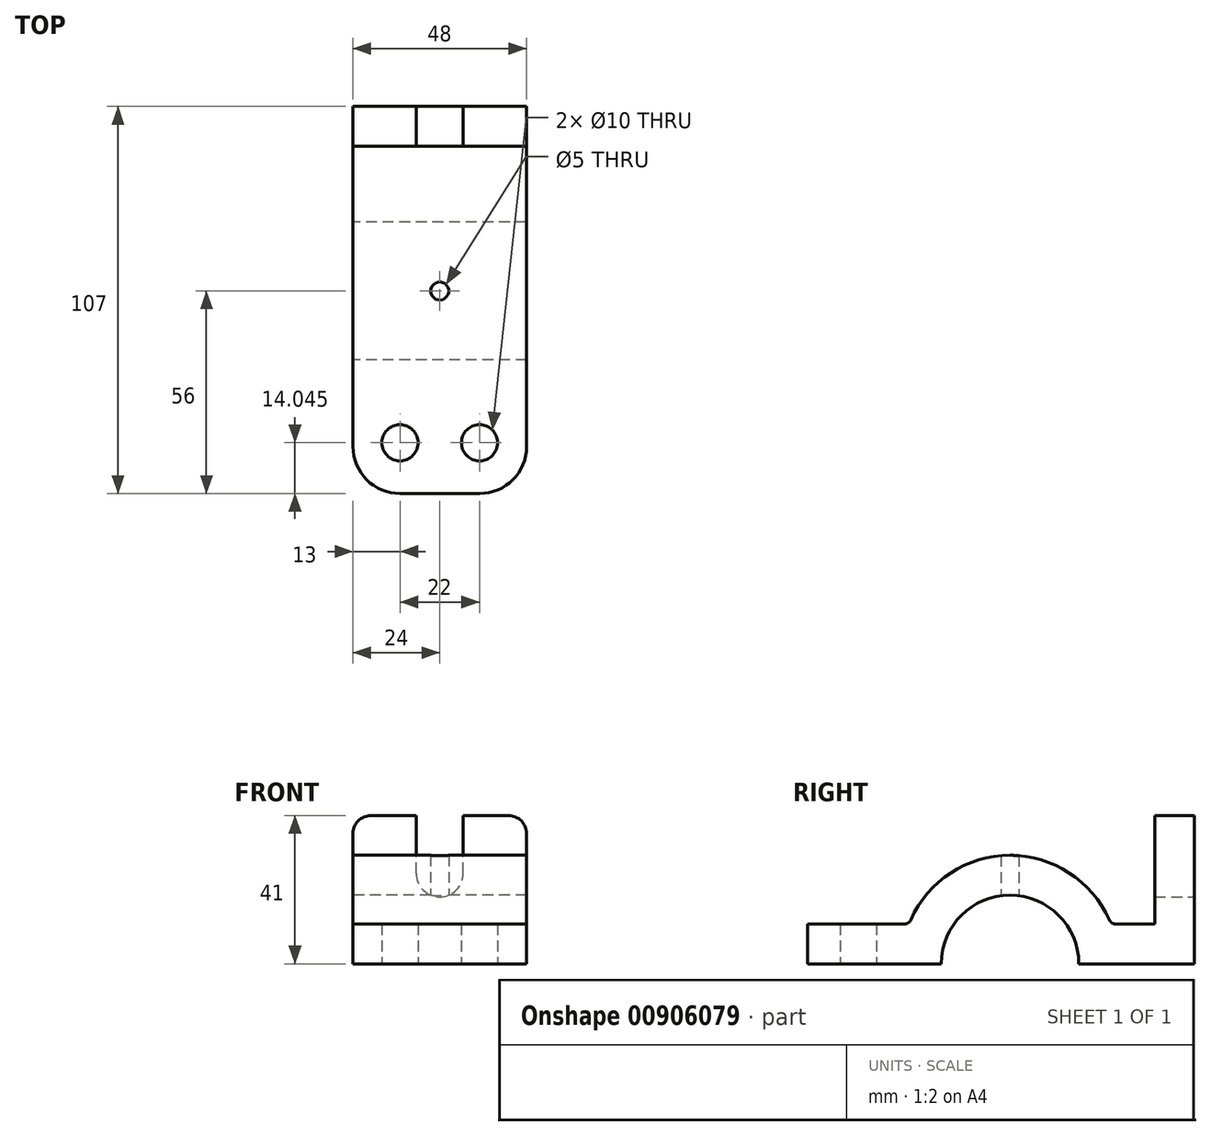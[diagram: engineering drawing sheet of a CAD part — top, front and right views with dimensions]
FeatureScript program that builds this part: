
annotation { "Feature Type Name" : "Feature", "Feature Type Description" : "" }
export const myFeature = defineFeature(function(context is Context, id is Id, definition is map)
    precondition{}
    {
        {
            var Q0;
            Q0=qCreatedBy(makeId("Right.planeOp"),FACE);
            var sketch = newSketch(context, id + "F0", { "sketchPlane" : qUnion([Q0])});
            skCircle(sketch, "E0", {"center": v(0, 0) * mm, "radius": 19 * mm});
            skCircle(sketch, "E1", {"center": v(0, 0) * mm, "radius": 30 * mm});
            skLineSegment(sketch, "E2.bottom", {"start": v(-56, 0) * mm, "end": v(51, 0) * mm});
            skLineSegment(sketch, "E2.top", {"start": v(-56, 11) * mm, "end": v(51, 11) * mm});
            skLineSegment(sketch, "E2.left", {"start": v(-56, 0) * mm, "end": v(-56, 11) * mm});
            skLineSegment(sketch, "E2.right", {"start": v(51, 0) * mm, "end": v(51, 11) * mm});
            skLineSegment(sketch, "E3.bottom", {"start": v(51, 11) * mm, "end": v(40, 11) * mm});
            skLineSegment(sketch, "E3.top", {"start": v(51, 41) * mm, "end": v(40, 41) * mm});
            skLineSegment(sketch, "E3.left", {"start": v(51, 11) * mm, "end": v(51, 41) * mm});
            skLineSegment(sketch, "E3.right", {"start": v(40, 11) * mm, "end": v(40, 41) * mm});
            skSolve(sketch);
        }
        {
            var Q0;
            {var subQ5=sQuery(id+"F0.wireOp",EDGE,"E2.left");Q0=makeQuery(id+"F0.imprint","IMPRINT",FACE,{"disambiguationData":[TD([[makeQuery(id+"F0.imprint","IMPRINT",EDGE,{"derivedFrom":subQ5}),-1.0]])]});}
            var Q1;
            {var subQ0=sQuery(id+"F0.wireOp",EDGE,"E2.bottom");var subQ1=sQuery(id+"F0.wireOp",EDGE,"E0");var subQ2=makeQuery(id+"F0.imprint","INTERSECT",VERTEX,{"disambiguationData":[OD(0.0)],"derivedFrom":[subQ1,subQ0]});Q1=makeQuery(id+"F0.imprint","IMPRINT",FACE,{"disambiguationData":[TD([[makeQuery(id+"F0.imprint","IMPRINT",EDGE,{"disambiguationData":[TD([[subQ2,1.0]])],"derivedFrom":subQ1}),-1.0]])]});}
            var Q2;
            {var subQ0=sQuery(id+"F0.wireOp",EDGE,"E2.top");var subQ1=sQuery(id+"F0.wireOp",EDGE,"E0");var subQ2=makeQuery(id+"F0.imprint","INTERSECT",VERTEX,{"disambiguationData":[OD(0.0)],"derivedFrom":[subQ1,subQ0]});Q2=makeQuery(id+"F0.imprint","IMPRINT",FACE,{"disambiguationData":[TD([[makeQuery(id+"F0.imprint","IMPRINT",EDGE,{"disambiguationData":[TD([[subQ2,1.0]])],"derivedFrom":subQ1}),-1.0]])]});}
            var Q3;
            {var subQ0=sQuery(id+"F0.wireOp",EDGE,"E2.top");var subQ1=sQuery(id+"F0.wireOp",EDGE,"E0");var subQ2=makeQuery(id+"F0.imprint","INTERSECT",VERTEX,{"disambiguationData":[OD(1.0)],"derivedFrom":[subQ1,subQ0]});Q3=makeQuery(id+"F0.imprint","IMPRINT",FACE,{"disambiguationData":[TD([[makeQuery(id+"F0.imprint","IMPRINT",EDGE,{"disambiguationData":[TD([[subQ2,1.0]])],"derivedFrom":subQ1}),-1.0]])]});}
            var Q4;
            {var subQ0=sQuery(id+"F0.wireOp",EDGE,"E2.right");Q4=makeQuery(id+"F0.imprint","IMPRINT",FACE,{"disambiguationData":[TD([[makeQuery(id+"F0.imprint","IMPRINT",EDGE,{"derivedFrom":subQ0}),1.0]])]});}
            var Q5;
            Q5=makeQuery(id+"F0.imprint","IMPRINT",FACE,{"disambiguationData":[TD([[makeQuery(id+"F0.imprint","IMPRINT",EDGE,{"derivedFrom":sQuery(id+"F0.wireOp",EDGE,"E3.top")}),1.0]])]});
            extrude(context, id + "F1", {"entities" : qUnion([Q0, Q1, Q2, Q3, Q4, Q5]), "endBound" : BoundingType.SYMMETRIC, "depth" : 48 * mm, "offsetDistance" : 25 * mm});
        }
        {
            var Q0;
            Q0=makeQuery(id+"F1.opExtrude","SWEPT_FACE",FACE,{"disambiguationData":[OSD([sQuery(id+"F0.wireOp",EDGE,"E2.right"),sQuery(id+"F0.wireOp",EDGE,"E3.left")])]});
            var sketch = newSketch(context, id + "F2", { "sketchPlane" : qUnion([Q0])});
            skLineSegment(sketch, "E4", {"start": v(0, 0) * mm, "end": v(0, 41) * mm, "construction": true});
            skCircle(sketch, "E5", {"center": v(0, 25) * mm, "radius": 6.5 * mm});
            skLineSegment(sketch, "E6", {"start": v(-6.5, 25) * mm, "end": v(-6.5, 41) * mm});
            skLineSegment(sketch, "E7", {"start": v(6.5, 25) * mm, "end": v(6.5, 41) * mm});
            skSolve(sketch);
        }
        {
            var Q0;
            {var subQ0=sQuery(id+"F2.wireOp",EDGE,"E5");var subQ2=makeQuery(id+"F2.imprint","INTERSECT",VERTEX,{"derivedFrom":[subQ0,sQuery(id+"F2.wireOp",EDGE,"E6")]});Q0=makeQuery(id+"F2.imprint","IMPRINT",FACE,{"disambiguationData":[TD([[makeQuery(id+"F2.imprint","IMPRINT",EDGE,{"disambiguationData":[TD([[subQ2,1.0]])],"derivedFrom":subQ0}),1.0]])]});}
            var Q1;
            {var subQ2=sQuery(id+"F2.wireOp",EDGE,"E6");Q1=makeQuery(id+"F2.imprint","IMPRINT",FACE,{"disambiguationData":[TD([[makeQuery(id+"F2.imprint","IMPRINT",EDGE,{"derivedFrom":subQ2}),-1.0]])]});}
            var Q2;
            Q2=makeQuery(id+"F1.opExtrude","SWEPT_FACE",FACE,{"disambiguationData":[OSD([sQuery(id+"F0.wireOp",EDGE,"E3.right")])]});
            extrude(context, id + "F3", {"entities" : qUnion([Q0, Q1]), "operationType" : NewBodyOperationType.REMOVE, "endBound" : BoundingType.UP_TO_SURFACE, "oppositeDirection" : true, "endBoundEntityFace" : qUnion([Q2]), "offsetDistance" : 25 * mm, "depth" : 25 * mm});
        }
        {
            var Q0;
            Q0=qCreatedBy(makeId("Top.planeOp"),FACE);
            var sketch = newSketch(context, id + "F4", { "sketchPlane" : qUnion([Q0])});
            skCircle(sketch, "E8", {"center": v(0, 0) * mm, "radius": 2.5 * mm});
            skLineSegment(sketch, "E9", {"start": v(24, -41.96) * mm, "end": v(-24, -41.96) * mm, "construction": true});
            skLineSegment(sketch, "E10", {"start": v(0, -56) * mm, "end": v(0, -27.91) * mm, "construction": true});
            skCircle(sketch, "E11", {"center": v(-11, -41.96) * mm, "radius": 5 * mm});
            skCircle(sketch, "E12", {"center": v(11, -41.96) * mm, "radius": 5 * mm});
            skSolve(sketch);
        }
        {
            var Q0;
            Q0=qSketchRegion(id+"F4",true);
            extrude(context, id + "F5", {"entities" : qUnion([Q0]), "operationType" : NewBodyOperationType.REMOVE, "endBound" : BoundingType.THROUGH_ALL, "depth" : 25 * mm});
        }
        {
            var Q0;
            Q0=makeQuery(id+"F1.opExtrude","CAP_EDGE",EDGE,{"disambiguationData":[OSD([sQuery(id+"F0.wireOp",EDGE,"E2.left")])],"isStart":false});
            var Q1;
            Q1=makeQuery(id+"F1.opExtrude","CAP_EDGE",EDGE,{"disambiguationData":[OSD([sQuery(id+"F0.wireOp",EDGE,"E2.left")])],"isStart":true});
            fillet(context, id + "F6", {"entities" : qUnion([Q0, Q1]), "radius" : 13 * mm, "tangentPropagation" : true, "allowEdgeOverflow" : false});
        }
        {
            var Q0;
            Q0=makeQuery(id+"F1.opExtrude","CAP_EDGE",EDGE,{"disambiguationData":[OSD([sQuery(id+"F0.wireOp",EDGE,"E3.top")])],"isStart":false});
            var Q1;
            Q1=makeQuery(id+"F1.opExtrude","CAP_EDGE",EDGE,{"disambiguationData":[OSD([sQuery(id+"F0.wireOp",EDGE,"E3.top")])],"isStart":true});
            fillet(context, id + "F7", {"entities" : qUnion([Q0, Q1]), "radius" : 5 * mm, "tangentPropagation" : true, "allowEdgeOverflow" : false});
        }
        {
            var Q0;
            {var subQ0=sQuery(id+"F0.wireOp",EDGE,"E2.top");var subQ1=sQuery(id+"F0.wireOp",EDGE,"E1");Q0=makeQuery(id+"F1.opExtrude","SWEPT_EDGE",EDGE,{"disambiguationData":[OSD([subQ1,subQ0]),TDD([makeQuery(id+"F0.imprint","INTERSECT",VERTEX,{"disambiguationData":[OD(1.0)],"derivedFrom":[subQ1,subQ0]})])]});}
            var Q1;
            {var subQ0=sQuery(id+"F0.wireOp",EDGE,"E2.top");var subQ1=sQuery(id+"F0.wireOp",EDGE,"E1");Q1=makeQuery(id+"F1.opExtrude","SWEPT_EDGE",EDGE,{"disambiguationData":[OSD([subQ1,subQ0]),TDD([makeQuery(id+"F0.imprint","INTERSECT",VERTEX,{"disambiguationData":[OD(0.0)],"derivedFrom":[subQ1,subQ0]})])]});}
            fillet(context, id + "F8", {"entities" : qUnion([Q0, Q1]), "radius" : 2 * mm, "tangentPropagation" : true, "allowEdgeOverflow" : false});
        }
    });
